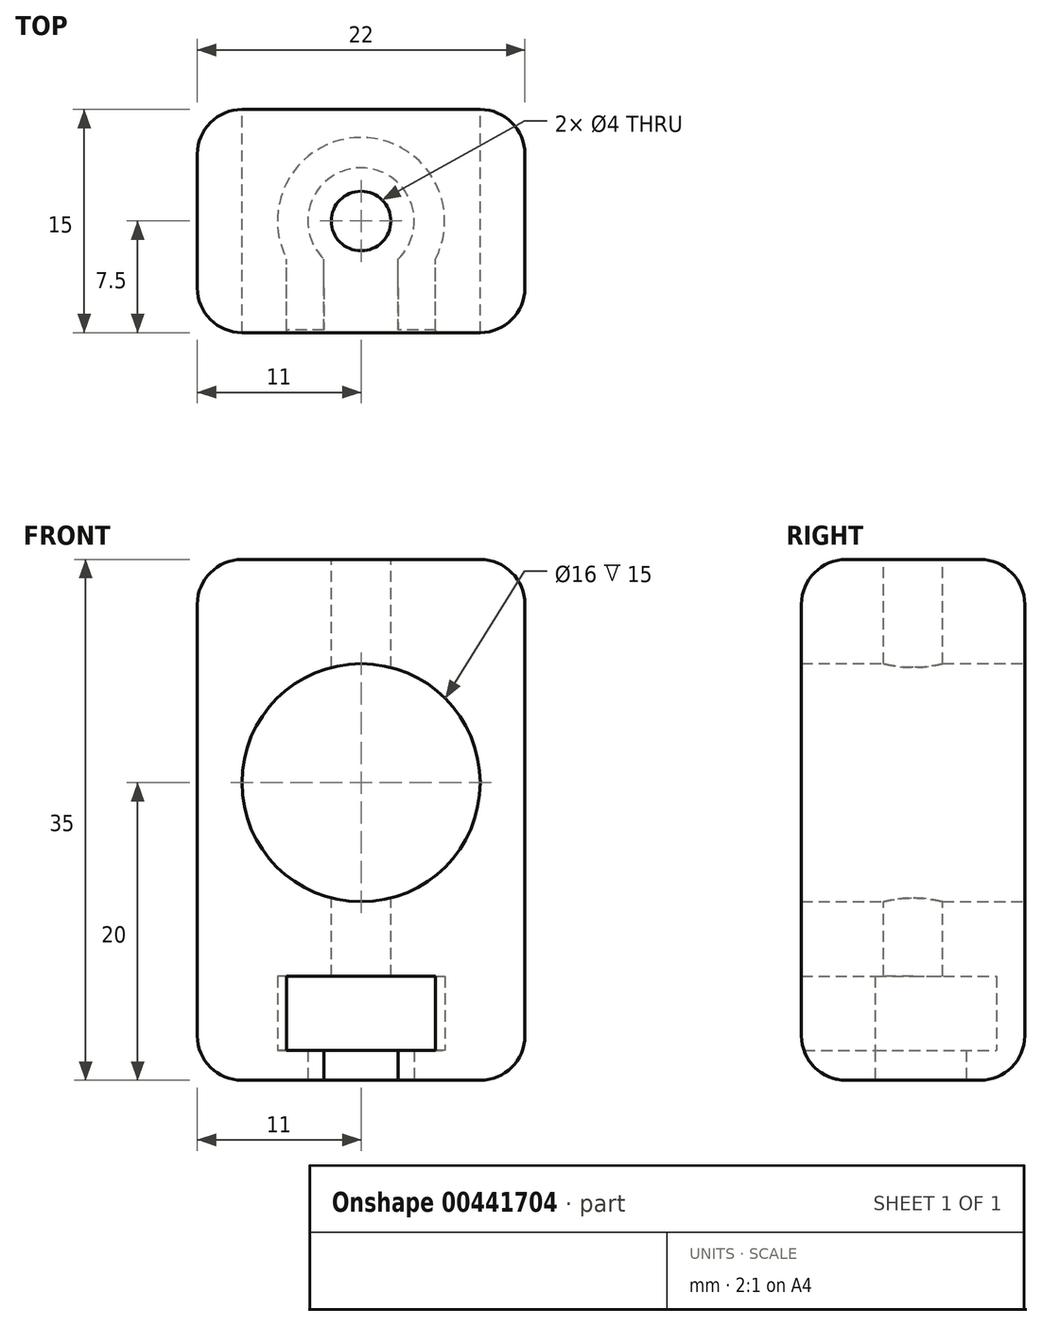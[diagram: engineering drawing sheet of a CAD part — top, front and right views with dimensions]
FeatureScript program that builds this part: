
annotation { "Feature Type Name" : "Feature", "Feature Type Description" : "" }
export const myFeature = defineFeature(function(context is Context, id is Id, definition is map)
    precondition{}
    {
        {
            var Q0;
            Q0=qCreatedBy(makeId("Front.planeOp"),FACE);
            var sketch = newSketch(context, id + "F0", { "sketchPlane" : qUnion([Q0])});
            skLineSegment(sketch, "E0.bottom", {"start": v(-11, -20) * mm, "end": v(11, -20) * mm});
            skLineSegment(sketch, "E0.top", {"start": v(-11, 15) * mm, "end": v(11, 15) * mm});
            skLineSegment(sketch, "E0.left", {"start": v(-11, -20) * mm, "end": v(-11, 15) * mm});
            skLineSegment(sketch, "E0.right", {"start": v(11, -20) * mm, "end": v(11, 15) * mm});
            skLineSegment(sketch, "E1", {"start": v(0, 18.36) * mm, "end": v(0, -15.6) * mm, "construction": true});
            skCircle(sketch, "E2", {"center": v(0, 0) * mm, "radius": 8 * mm});
            skLineSegment(sketch, "E3", {"start": v(-58.12, -2.5) * mm, "end": v(61.9, -2.5) * mm, "construction": true});
            skSolve(sketch);
        }
        {
            var Q0;
            Q0=qSketchRegion(id+"F0",true);
            extrude(context, id + "F1", {"entities" : qUnion([Q0]), "endBound" : BoundingType.SYMMETRIC, "depth" : 15 * mm});
        }
        {
            var Q0;
            Q0=makeQuery(id+"F1.opExtrude","SWEPT_FACE",FACE,{"disambiguationData":[OSD([sQuery(id+"F0.wireOp",EDGE,"E0.bottom")])]});
            var sketch = newSketch(context, id + "F2", { "sketchPlane" : qUnion([Q0])});
            skLineSegment(sketch, "E4", {"start": v(-2.5, 7.5) * mm, "end": v(-2.5, 2.56) * mm});
            skLineSegment(sketch, "E5", {"start": v(2.5, 7.5) * mm, "end": v(2.5, 2.56) * mm});
            skArc(sketch, "E6", {"start": v(-2.5, 2.56) * mm, "mid": v(0, -3.58) * mm, "end": v(2.5, 2.56) * mm});
            skLineSegment(sketch, "E7", {"start": v(0, 10.7) * mm, "end": v(0, -12.84) * mm, "construction": true});
            skSolve(sketch);
        }
        {
            var Q0;
            Q0=qSketchRegion(id+"F2",true);
            var Q1;
            {var subQ0=sQuery(id+"F2.wireOp",EDGE,"E4");Q1=makeQuery(id+"F2.imprint","IMPRINT",FACE,{"disambiguationData":[TD([[makeQuery(id+"F2.imprint","IMPRINT",EDGE,{"derivedFrom":subQ0}),1.0]])]});}
            extrude(context, id + "F3", {"entities" : qUnion([Q0, Q1]), "operationType" : NewBodyOperationType.REMOVE, "oppositeDirection" : true, "depth" : 2 * mm});
        }
        {
            var Q0;
            Q0=makeQuery(id+"F1.opExtrude","SWEPT_FACE",FACE,{"disambiguationData":[OSD([sQuery(id+"F0.wireOp",EDGE,"E0.bottom")])]});
            cPlane(context, id + "F4", {"entities" : qUnion([Q0]), "cplaneType" : CPlaneType.OFFSET, "offset" : 2 * mm, "oppositeDirection" : true, "width" : 150 * mm, "height" : 150 * mm});
        }
        {
            var Q0;
            Q0=qCreatedBy(id+"F4.planeOp",FACE);
            var sketch = newSketch(context, id + "F5", { "sketchPlane" : qUnion([Q0])});
            skLineSegment(sketch, "E8", {"start": v(-5, 7.5) * mm, "end": v(-5, 2.56) * mm});
            skLineSegment(sketch, "E9", {"start": v(5, 7.5) * mm, "end": v(5, 2.56) * mm});
            skLineSegment(sketch, "E10", {"start": v(0, 11.6) * mm, "end": v(0, -12.84) * mm, "construction": true});
            skArc(sketch, "E11", {"start": v(-5, 2.56) * mm, "mid": v(0, -5.62) * mm, "end": v(5, 2.56) * mm});
            skLineSegment(sketch, "E12", {"start": v(-5, 7.5) * mm, "end": v(5, 7.5) * mm});
            skSolve(sketch);
        }
        {
            var Q0;
            Q0=qSketchRegion(id+"F5",true);
            extrude(context, id + "F6", {"entities" : qUnion([Q0]), "operationType" : NewBodyOperationType.REMOVE, "oppositeDirection" : true, "depth" : 5 * mm, "offsetDistance" : 25 * mm});
        }
        {
            var Q0;
            Q0=makeQuery(id+"F1.opExtrude","SWEPT_FACE",FACE,{"disambiguationData":[OSD([sQuery(id+"F0.wireOp",EDGE,"E0.top")])]});
            var sketch = newSketch(context, id + "F7", { "sketchPlane" : qUnion([Q0])});
            skCircle(sketch, "E13", {"center": v(0, 0) * mm, "radius": 2 * mm});
            skSolve(sketch);
        }
        {
            var Q0;
            Q0=makeQuery(id+"F7.imprint","IMPRINT",FACE,{"disambiguationData":[TD([[makeQuery(id+"F7.imprint","IMPRINT",EDGE,{"derivedFrom":sQuery(id+"F7.wireOp",EDGE,"E13")}),1.0]])]});
            extrude(context, id + "F8", {"entities" : qUnion([Q0]), "operationType" : NewBodyOperationType.REMOVE, "endBound" : BoundingType.THROUGH_ALL, "oppositeDirection" : true, "depth" : 6 * mm});
        }
        {
            var Q0;
            Q0=makeQuery(id+"F1.opExtrude","SWEPT_EDGE",EDGE,{"disambiguationData":[OSD([sQuery(id+"F0.wireOp",EDGE,"E0.top"),sQuery(id+"F0.wireOp",EDGE,"E0.left")])]});
            var Q1;
            Q1=makeQuery(id+"F1.opExtrude","SWEPT_EDGE",EDGE,{"disambiguationData":[OSD([sQuery(id+"F0.wireOp",EDGE,"E0.top"),sQuery(id+"F0.wireOp",EDGE,"E0.right")])]});
            var Q2;
            Q2=makeQuery(id+"F1.opExtrude","CAP_EDGE",EDGE,{"disambiguationData":[OSD([sQuery(id+"F0.wireOp",EDGE,"E0.top")])],"isStart":false});
            var Q3;
            Q3=makeQuery(id+"F1.opExtrude","CAP_EDGE",EDGE,{"disambiguationData":[OSD([sQuery(id+"F0.wireOp",EDGE,"E0.top")])],"isStart":true});
            var Q4;
            Q4=makeQuery(id+"F1.opExtrude","CAP_EDGE",EDGE,{"disambiguationData":[OSD([sQuery(id+"F0.wireOp",EDGE,"E0.right")])],"isStart":false});
            var Q5;
            Q5=makeQuery(id+"F1.opExtrude","CAP_EDGE",EDGE,{"disambiguationData":[OSD([sQuery(id+"F0.wireOp",EDGE,"E0.left")])],"isStart":false});
            var Q6;
            Q6=makeQuery(id+"F1.opExtrude","CAP_EDGE",EDGE,{"disambiguationData":[OSD([sQuery(id+"F0.wireOp",EDGE,"E0.left")])],"isStart":true});
            var Q7;
            Q7=makeQuery(id+"F1.opExtrude","CAP_EDGE",EDGE,{"disambiguationData":[OSD([sQuery(id+"F0.wireOp",EDGE,"E0.right")])],"isStart":true});
            var Q8;
            Q8=makeQuery(id+"F1.opExtrude","CAP_EDGE",EDGE,{"disambiguationData":[OSD([sQuery(id+"F0.wireOp",EDGE,"E0.bottom")])],"isStart":true});
            var Q9;
            {var subQ0=sQuery(id+"F0.wireOp",EDGE,"E0.bottom");var subQ1=sQuery(id+"F0.wireOp",EDGE,"E0.left");Q9=makeQuery(id+"F3.boolean.opBoolean","SPLIT",EDGE,{"disambiguationData":[TD([makeQuery(id+"F1.opExtrude","SWEPT_FACE",FACE,{"disambiguationData":[OSD([subQ1])]})])],"derivedFrom":makeQuery(id+"F1.opExtrude","CAP_EDGE",EDGE,{"disambiguationData":[OSD([subQ0])],"isStart":false})});}
            var Q10;
            {var subQ0=sQuery(id+"F0.wireOp",EDGE,"E0.bottom");var subQ1=sQuery(id+"F0.wireOp",EDGE,"E0.right");Q10=makeQuery(id+"F3.boolean.opBoolean","SPLIT",EDGE,{"disambiguationData":[TD([makeQuery(id+"F1.opExtrude","SWEPT_FACE",FACE,{"disambiguationData":[OSD([subQ1])]})])],"derivedFrom":makeQuery(id+"F1.opExtrude","CAP_EDGE",EDGE,{"disambiguationData":[OSD([subQ0])],"isStart":false})});}
            var Q11;
            Q11=makeQuery(id+"F1.opExtrude","SWEPT_EDGE",EDGE,{"disambiguationData":[OSD([sQuery(id+"F0.wireOp",EDGE,"E0.bottom"),sQuery(id+"F0.wireOp",EDGE,"E0.left")])]});
            var Q12;
            Q12=makeQuery(id+"F1.opExtrude","SWEPT_EDGE",EDGE,{"disambiguationData":[OSD([sQuery(id+"F0.wireOp",EDGE,"E0.bottom"),sQuery(id+"F0.wireOp",EDGE,"E0.right")])]});
            fillet(context, id + "F9", {"entities" : qUnion([Q0, Q1, Q2, Q3, Q4, Q5, Q6, Q7, Q8, Q9, Q10, Q11, Q12]), "radius" : 3 * mm, "tangentPropagation" : true, "allowEdgeOverflow" : false});
        }
    });
